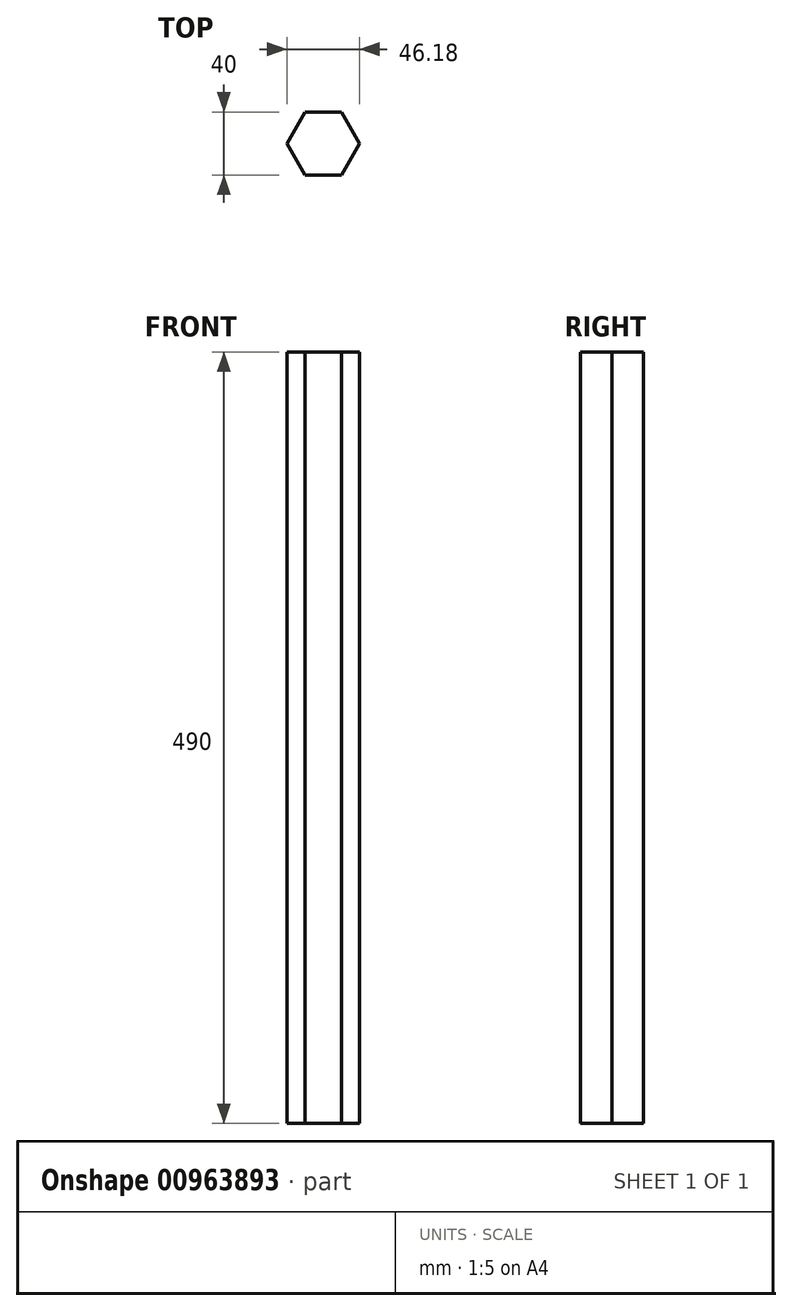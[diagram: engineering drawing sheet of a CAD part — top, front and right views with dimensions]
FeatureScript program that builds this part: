
annotation { "Feature Type Name" : "Feature", "Feature Type Description" : "" }
export const myFeature = defineFeature(function(context is Context, id is Id, definition is map)
    precondition{}
    {
        {
            var Q0;
            Q0=qCreatedBy(makeId("Top.planeOp"),FACE);
            var sketch = newSketch(context, id + "F0", { "sketchPlane" : qUnion([Q0])});
            skCircle(sketch, "E0.cCircle", {"center": v(0, 0) * mm, "radius": 20 * mm, "construction": true});
            skLineSegment(sketch, "E0.0", {"start": v(-11.55, 20) * mm, "end": v(11.55, 20) * mm});
            skLineSegment(sketch, "E0.1", {"start": v(11.55, 20) * mm, "end": v(23.1, 0) * mm});
            skLineSegment(sketch, "E0.2", {"start": v(23.1, 0) * mm, "end": v(11.55, -20) * mm});
            skLineSegment(sketch, "E0.3", {"start": v(11.55, -20) * mm, "end": v(-11.55, -20) * mm});
            skLineSegment(sketch, "E0.4", {"start": v(-11.55, -20) * mm, "end": v(-23.1, 0) * mm});
            skLineSegment(sketch, "E0.5", {"start": v(-23.1, 0) * mm, "end": v(-11.55, 20) * mm});
            skPoint(sketch, "E0.0.midPoint", {"position": v(0, 20) * mm});
            skSolve(sketch);
        }
        {
            var Q0;
            Q0=makeQuery(id+"F0.imprint","IMPRINT",FACE,{"disambiguationData":[TD([[makeQuery(id+"F0.imprint","IMPRINT",EDGE,{"derivedFrom":sQuery(id+"F0.wireOp",EDGE,"E0.0")}),-1.0]])]});
            extrude(context, id + "F1", {"entities" : qUnion([Q0]), "depth" : 490 * mm, "offsetDistance" : 25.4 * mm});
        }
    });
